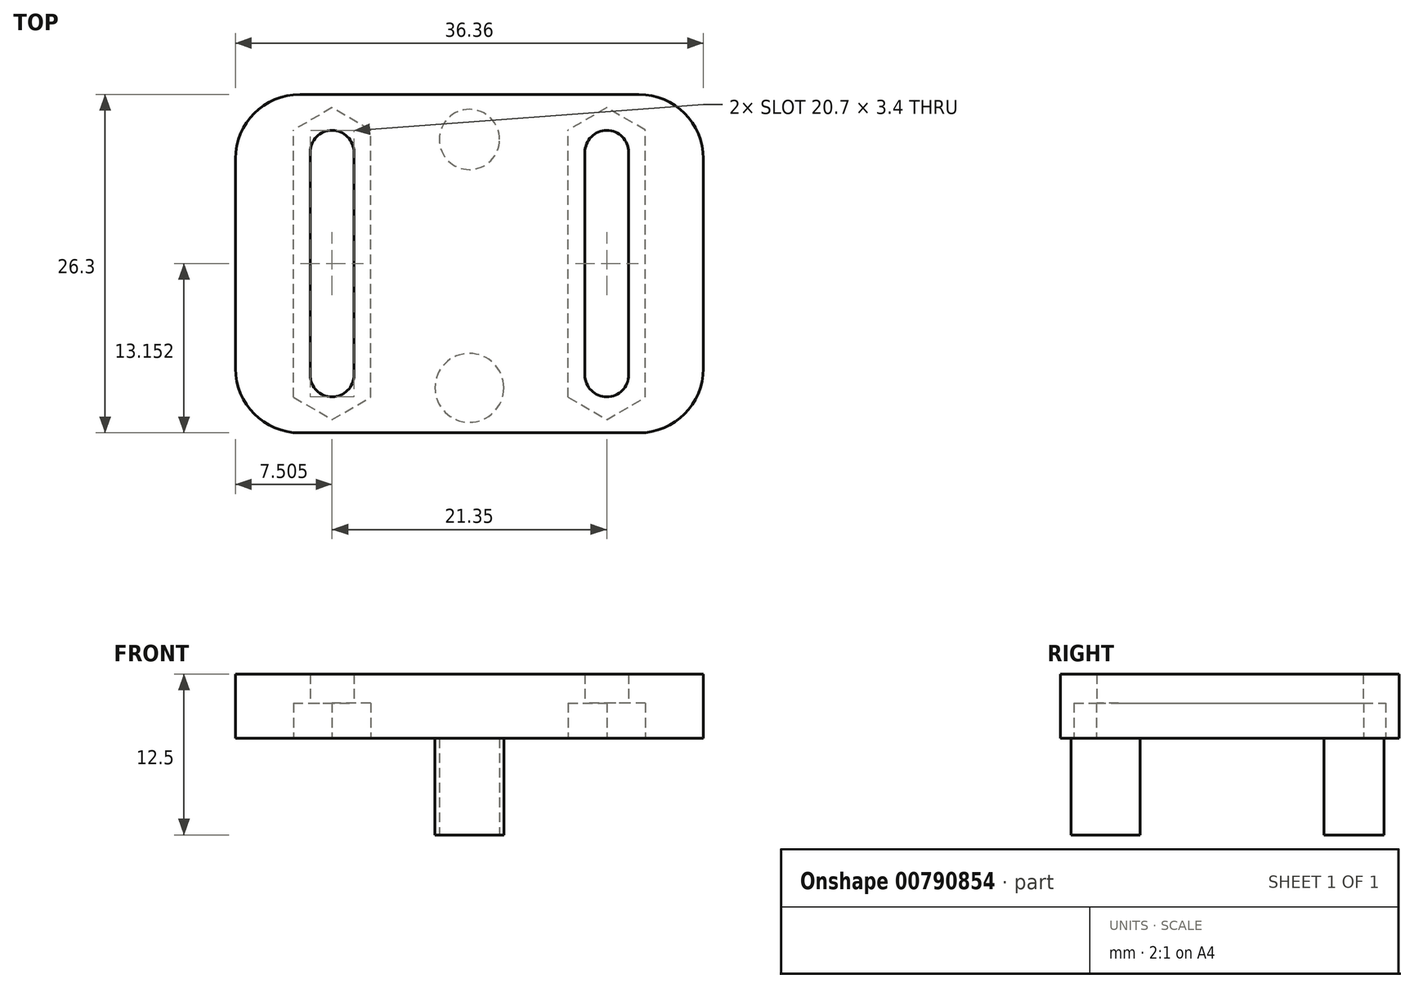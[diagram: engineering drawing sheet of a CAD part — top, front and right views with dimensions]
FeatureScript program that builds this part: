
annotation { "Feature Type Name" : "Feature", "Feature Type Description" : "" }
export const myFeature = defineFeature(function(context is Context, id is Id, definition is map)
    precondition{}
    {
        {
            var Q0;
            Q0=qCreatedBy(makeId("Top.planeOp"),FACE);
            var sketch = newSketch(context, id + "F0", { "sketchPlane" : qUnion([Q0])});
            skCircle(sketch, "E0", {"center": v(0, 0) * mm, "radius": 2.67 * mm});
            skCircle(sketch, "E1", {"center": v(0, 19.3) * mm, "radius": 2.34 * mm});
            skLineSegment(sketch, "E2.bottom", {"start": v(0, 9.65) * mm, "end": v(82.65, 9.65) * mm});
            skLineSegment(sketch, "E2.top", {"start": v(0, 230.05) * mm, "end": v(82.65, 230.05) * mm});
            skLineSegment(sketch, "E2.left", {"start": v(0, 9.65) * mm, "end": v(0, 230.05) * mm});
            skLineSegment(sketch, "E2.right", {"start": v(82.65, 9.65) * mm, "end": v(82.65, 230.05) * mm});
            skLineSegment(sketch, "E3", {"start": v(0, 19.3) * mm, "end": v(0, 0) * mm});
            skPoint(sketch, "E4", {"position": v(0, 9.65) * mm});
            skCircle(sketch, "E5.0.1.0", {"center": v(0, 239.7) * mm, "radius": 2.34 * mm});
            skCircle(sketch, "E5.0.1.1", {"center": v(0, 220.4) * mm, "radius": 2.67 * mm});
            skCircle(sketch, "E5.1.0.0", {"center": v(82.65, 19.3) * mm, "radius": 2.34 * mm});
            skCircle(sketch, "E5.1.0.1", {"center": v(82.65, 0) * mm, "radius": 2.67 * mm});
            skCircle(sketch, "E5.1.1.0", {"center": v(82.65, 239.7) * mm, "radius": 2.34 * mm});
            skCircle(sketch, "E5.1.1.1", {"center": v(82.65, 220.4) * mm, "radius": 2.67 * mm});
            skLineSegment(sketch, "E5.direction1", {"start": v(0, 19.3) * mm, "end": v(82.65, 19.3) * mm, "construction": true});
            skLineSegment(sketch, "E5.direction2", {"start": v(0, 19.3) * mm, "end": v(0, 239.7) * mm, "construction": true});
            skLineSegment(sketch, "E6.bottom", {"start": v(-10.68, 203.05) * mm, "end": v(93.32, 203.05) * mm});
            skLineSegment(sketch, "E6.top", {"start": v(-10.68, 35.05) * mm, "end": v(93.32, 35.05) * mm});
            skLineSegment(sketch, "E6.left", {"start": v(-10.68, 203.05) * mm, "end": v(-10.68, 35.05) * mm});
            skLineSegment(sketch, "E6.right", {"start": v(93.32, 203.05) * mm, "end": v(93.32, 35.05) * mm});
            skCircle(sketch, "E7.0.1.0", {"center": v(82.65, 27.55) * mm, "radius": 2.67 * mm});
            skCircle(sketch, "E7.0.1.1", {"center": v(82.65, 46.86) * mm, "radius": 2.34 * mm});
            skCircle(sketch, "E7.0.1.2", {"center": v(0, 46.85) * mm, "radius": 2.34 * mm});
            skCircle(sketch, "E7.0.1.3", {"center": v(0, 27.55) * mm, "radius": 2.67 * mm});
            skLineSegment(sketch, "E7.direction1", {"start": v(0, 0) * mm, "end": v(25, 0) * mm, "construction": true});
            skLineSegment(sketch, "E7.direction2", {"start": v(0, 0) * mm, "end": v(0, 27.55) * mm, "construction": true});
            skCircle(sketch, "E8.0.1.0", {"center": v(0, 192.85) * mm, "radius": 2.67 * mm});
            skCircle(sketch, "E8.0.1.1", {"center": v(82.65, 192.85) * mm, "radius": 2.67 * mm});
            skCircle(sketch, "E8.0.1.2", {"center": v(0, 212.16) * mm, "radius": 2.34 * mm});
            skCircle(sketch, "E8.0.1.3", {"center": v(82.65, 212.16) * mm, "radius": 2.34 * mm});
            skLineSegment(sketch, "E8.direction1", {"start": v(0, 220.4) * mm, "end": v(25, 220.4) * mm, "construction": true});
            skLineSegment(sketch, "E8.direction2", {"start": v(0, 220.4) * mm, "end": v(0, 192.85) * mm, "construction": true});
            skPoint(sketch, "E9", {"position": v(93.32, 37.75) * mm});
            skSolve(sketch);
        }
        {
            var Q0;
            Q0=qCreatedBy(makeId("Top.planeOp"),FACE);
            var sketch = newSketch(context, id + "F1", { "sketchPlane" : qUnion([Q0])});
            skCircle(sketch, "E10.0", {"center": v(0, 19.3) * mm, "radius": 2.34 * mm});
            skCircle(sketch, "E11.0", {"center": v(0, 0) * mm, "radius": 2.67 * mm});
            skSolve(sketch);
        }
        {
            var Q0;
            Q0=qSketchRegion(id+"F1",true);
            extrude(context, id + "F2", {"entities" : qUnion([Q0]), "depth" : 7.5 * mm, "offsetDistance" : 25 * mm});
        }
        {
            var Q0;
            Q0=makeQuery(id+"F2.opExtrude","CAP_FACE",FACE,{"disambiguationData":[OSD([sQuery(id+"F1.wireOp",EDGE,"E10.0")])],"isStart":false});
            var sketch = newSketch(context, id + "F3", { "sketchPlane" : qUnion([Q0])});
            skPoint(sketch, "E12.0", {"position": v(82.65, 27.55) * mm});
            skPoint(sketch, "E13.0", {"position": v(82.65, 46.86) * mm});
            skPoint(sketch, "E14.0", {"position": v(93.32, 37.75) * mm});
            skPoint(sketch, "E15.0", {"position": v(93.32, 35.05) * mm});
            skLineSegment(sketch, "E16.bottom", {"start": v(0, 22.8) * mm, "end": v(-10.68, 22.8) * mm});
            skLineSegment(sketch, "E16.top", {"start": v(0, -3.5) * mm, "end": v(-10.67, -3.5) * mm});
            skLineSegment(sketch, "E16.left", {"start": v(0, 22.8) * mm, "end": v(0, -3.5) * mm});
            skLineSegment(sketch, "E16.right", {"start": v(-10.68, 22.8) * mm, "end": v(-10.67, -3.5) * mm});
            skPoint(sketch, "E17", {"position": v(0, 19.3) * mm});
            skPoint(sketch, "E18", {"position": v(0, 0) * mm});
            skLineSegment(sketch, "E19.bottom", {"start": v(0, 22.8) * mm, "end": v(10.68, 22.8) * mm});
            skLineSegment(sketch, "E19.top", {"start": v(0, -3.5) * mm, "end": v(10.68, -3.5) * mm});
            skLineSegment(sketch, "E19.right", {"start": v(10.68, 22.8) * mm, "end": v(10.68, -3.5) * mm});
            skLineSegment(sketch, "E20.bottom", {"start": v(-10.68, 22.8) * mm, "end": v(-18.18, 22.8) * mm});
            skLineSegment(sketch, "E20.top", {"start": v(-10.67, -3.5) * mm, "end": v(-18.17, -3.5) * mm});
            skLineSegment(sketch, "E20.right", {"start": v(-18.18, 22.8) * mm, "end": v(-18.17, -3.5) * mm});
            skPoint(sketch, "E21", {"position": v(-10.67, 1) * mm});
            skPoint(sketch, "E22", {"position": v(-10.68, 18.3) * mm});
            skLineSegment(sketch, "E23.bottom", {"start": v(10.68, 22.8) * mm, "end": v(18.18, 22.8) * mm});
            skLineSegment(sketch, "E23.top", {"start": v(10.68, -3.5) * mm, "end": v(18.18, -3.5) * mm});
            skLineSegment(sketch, "E23.right", {"start": v(18.18, 22.8) * mm, "end": v(18.18, -3.5) * mm});
            skPoint(sketch, "E24", {"position": v(10.68, 1) * mm});
            skPoint(sketch, "E25", {"position": v(10.68, 18.3) * mm});
            skCircle(sketch, "E26", {"center": v(-10.68, 18.3) * mm, "radius": 1.7 * mm});
            skCircle(sketch, "E27", {"center": v(10.68, 18.3) * mm, "radius": 1.7 * mm});
            skCircle(sketch, "E28", {"center": v(10.68, 1) * mm, "radius": 1.7 * mm});
            skCircle(sketch, "E29", {"center": v(-10.67, 1) * mm, "radius": 1.7 * mm});
            skLineSegment(sketch, "E30", {"start": v(-8.97, 18.3) * mm, "end": v(-8.97, 1) * mm});
            skLineSegment(sketch, "E31", {"start": v(8.97, 18.3) * mm, "end": v(8.97, 1) * mm});
            skLineSegment(sketch, "E32", {"start": v(-12.37, 18.3) * mm, "end": v(-12.37, 1) * mm});
            skLineSegment(sketch, "E33", {"start": v(12.38, 1) * mm, "end": v(12.38, 18.3) * mm});
            skSolve(sketch);
        }
        {
            var Q0;
            Q0=makeQuery(id+"F3.imprint","IMPRINT",FACE,{"disambiguationData":[TD([[makeQuery(id+"F3.imprint","IMPRINT",EDGE,{"derivedFrom":makeQuery(id+"F2.opExtrude","CAP_EDGE",EDGE,{"disambiguationData":[OSD([sQuery(id+"F0.wireOp",EDGE,"E1")])],"isStart":false})}),-1.0]])]});
            var Q1;
            {var subQ0=sQuery(id+"F3.wireOp",EDGE,"TZnfkHZf-DKkp-xptn-AsGC-FlYiCB8cDqTM");Q1=makeQuery(id+"F3.imprint","IMPRINT",FACE,{"disambiguationData":[TD([[makeQuery(id+"F3.imprint","IMPRINT",EDGE,{"derivedFrom":subQ0}),-1.0]])]});}
            var Q2;
            {var subQ0=sQuery(id+"F3.wireOp",EDGE,"XSsqlgjZ-LNJ9-Avoh-l53S-mxeqoTWxBHOC");var subQ1=makeQuery(id+"F3.imprint","INTERSECT",VERTEX,{"derivedFrom":[subQ0,sQuery(id+"F3.wireOp",EDGE,"TZnfkHZf-DKkp-xptn-AsGC-FlYiCB8cDqTM")]});Q2=makeQuery(id+"F3.imprint","IMPRINT",FACE,{"disambiguationData":[TD([[makeQuery(id+"F3.imprint","IMPRINT",EDGE,{"disambiguationData":[TD([[subQ1,1.0]])],"derivedFrom":subQ0}),1.0]])]});}
            var Q3;
            Q3=makeQuery(id+"F3.imprint","IMPRINT",FACE,{"disambiguationData":[TD([[makeQuery(id+"F3.imprint","IMPRINT",EDGE,{"derivedFrom":makeQuery(id+"F2.opExtrude","CAP_EDGE",EDGE,{"disambiguationData":[OSD([sQuery(id+"F0.wireOp",EDGE,"E1")])],"isStart":false})}),1.0]])]});
            var Q4;
            Q4=makeQuery(id+"F3.imprint","IMPRINT",FACE,{"disambiguationData":[TD([[makeQuery(id+"F3.imprint","IMPRINT",EDGE,{"derivedFrom":sQuery(id+"F3.wireOp",EDGE,"hKwLHGTs-qPJH-S5hr-Gcpr-7g2Lq1g5tTZc.bottom")}),1.0]])]});
            var Q5;
            Q5=makeQuery(id+"F3.imprint","IMPRINT",FACE,{"disambiguationData":[TD([[makeQuery(id+"F3.imprint","IMPRINT",EDGE,{"derivedFrom":sQuery(id+"F3.wireOp",EDGE,"hKwLHGTs-qPJH-S5hr-Gcpr-7g2Lq1g5tTZc.bottom")}),-1.0]])]});
            var Q6;
            Q6=makeQuery(id+"F3.imprint","IMPRINT",FACE,{"disambiguationData":[TD([[makeQuery(id+"F3.imprint","IMPRINT",EDGE,{"derivedFrom":sQuery(id+"F3.wireOp",EDGE,"S0UTHaCf-9Zco-C6hI-kq23-d3yPxSgRmCOZ.bottom")}),1.0]])]});
            var Q7;
            Q7=makeQuery(id+"F3.imprint","IMPRINT",FACE,{"disambiguationData":[TD([[makeQuery(id+"F3.imprint","IMPRINT",EDGE,{"derivedFrom":makeQuery(id+"F2.opExtrude","CAP_EDGE",EDGE,{"disambiguationData":[OSD([sQuery(id+"F1.wireOp",EDGE,"E10.0")])],"isStart":false})}),1.0]])]});
            var Q8;
            {var subQ3=sQuery(id+"F3.wireOp",EDGE,"dA8Uuovx-4eO9-e5tU-pRAa-RQbBhlRNXynu.bottom");Q8=makeQuery(id+"F3.imprint","IMPRINT",FACE,{"disambiguationData":[TD([[makeQuery(id+"F3.imprint","IMPRINT",EDGE,{"derivedFrom":subQ3}),-1.0]])]});}
            var Q9;
            Q9=makeQuery(id+"F3.imprint","IMPRINT",FACE,{"disambiguationData":[TD([[makeQuery(id+"F3.imprint","IMPRINT",EDGE,{"derivedFrom":sQuery(id+"F3.wireOp",EDGE,"pLl2V4uJ-uvpy-u4wN-YW1n-wzNoaj7xdnqu.bottom")}),-1.0]])]});
            var Q10;
            Q10=makeQuery(id+"F3.imprint","IMPRINT",FACE,{"disambiguationData":[TD([[makeQuery(id+"F3.imprint","IMPRINT",EDGE,{"derivedFrom":sQuery(id+"F3.wireOp",EDGE,"rTHW2GkA-8Re8-zC11-azSP-cnDfZQFP3jBD.bottom")}),1.0]])]});
            var Q11;
            {var subQ3=sQuery(id+"F3.wireOp",EDGE,"04D0zXul-GAz9-AviL-uxYt-cow7iv5wdFvi.bottom");Q11=makeQuery(id+"F3.imprint","IMPRINT",FACE,{"disambiguationData":[TD([[makeQuery(id+"F3.imprint","IMPRINT",EDGE,{"derivedFrom":subQ3}),1.0]])]});}
            var Q12;
            {var subQ4=sQuery(id+"F3.wireOp",EDGE,"E19.bottom");Q12=makeQuery(id+"F3.imprint","IMPRINT",FACE,{"disambiguationData":[TD([[makeQuery(id+"F3.imprint","IMPRINT",EDGE,{"derivedFrom":subQ4}),-1.0]])]});}
            var Q13;
            {var subQ1=sQuery(id+"F3.wireOp",EDGE,"E16.bottom");Q13=makeQuery(id+"F3.imprint","IMPRINT",FACE,{"disambiguationData":[TD([[makeQuery(id+"F3.imprint","IMPRINT",EDGE,{"derivedFrom":subQ1}),1.0]])]});}
            var Q14;
            Q14=makeQuery(id+"F3.imprint","IMPRINT",FACE,{"disambiguationData":[TD([[makeQuery(id+"F3.imprint","IMPRINT",EDGE,{"derivedFrom":sQuery(id+"F3.wireOp",EDGE,"E20.bottom")}),1.0]])]});
            var Q15;
            Q15=makeQuery(id+"F3.imprint","IMPRINT",FACE,{"disambiguationData":[TD([[makeQuery(id+"F3.imprint","IMPRINT",EDGE,{"derivedFrom":sQuery(id+"F3.wireOp",EDGE,"E23.bottom")}),-1.0]])]});
            extrude(context, id + "F4", {"entities" : qUnion([Q0, Q1, Q2, Q3, Q4, Q5, Q6, Q7, Q8, Q9, Q10, Q11, Q12, Q13, Q14, Q15]), "depth" : 5 * mm, "offsetDistance" : 25 * mm});
        }
        {
            var Q0;
            Q0=makeQuery(id+"F4.opExtrude","SWEPT_EDGE",EDGE,{"disambiguationData":[OSD([sQuery(id+"F3.wireOp",EDGE,"hKwLHGTs-qPJH-S5hr-Gcpr-7g2Lq1g5tTZc.top"),sQuery(id+"F3.wireOp",EDGE,"hKwLHGTs-qPJH-S5hr-Gcpr-7g2Lq1g5tTZc.left")])]});
            var Q1;
            Q1=makeQuery(id+"F4.opExtrude","SWEPT_EDGE",EDGE,{"disambiguationData":[OSD([sQuery(id+"F3.wireOp",EDGE,"hKwLHGTs-qPJH-S5hr-Gcpr-7g2Lq1g5tTZc.top"),sQuery(id+"F3.wireOp",EDGE,"hKwLHGTs-qPJH-S5hr-Gcpr-7g2Lq1g5tTZc.right")])]});
            var Q2;
            Q2=makeQuery(id+"F4.opExtrude","SWEPT_EDGE",EDGE,{"disambiguationData":[OSD([sQuery(id+"F3.wireOp",EDGE,"S0UTHaCf-9Zco-C6hI-kq23-d3yPxSgRmCOZ.top"),sQuery(id+"F3.wireOp",EDGE,"S0UTHaCf-9Zco-C6hI-kq23-d3yPxSgRmCOZ.right")])]});
            var Q3;
            Q3=makeQuery(id+"F4.opExtrude","SWEPT_EDGE",EDGE,{"disambiguationData":[OSD([sQuery(id+"F3.wireOp",EDGE,"S0UTHaCf-9Zco-C6hI-kq23-d3yPxSgRmCOZ.top"),sQuery(id+"F3.wireOp",EDGE,"S0UTHaCf-9Zco-C6hI-kq23-d3yPxSgRmCOZ.left")])]});
            var Q4;
            Q4=makeQuery(id+"F4.opExtrude","SWEPT_EDGE",EDGE,{"disambiguationData":[OSD([sQuery(id+"F3.wireOp",EDGE,"pLl2V4uJ-uvpy-u4wN-YW1n-wzNoaj7xdnqu.bottom"),sQuery(id+"F3.wireOp",EDGE,"pLl2V4uJ-uvpy-u4wN-YW1n-wzNoaj7xdnqu.right")])]});
            var Q5;
            Q5=makeQuery(id+"F4.opExtrude","SWEPT_EDGE",EDGE,{"disambiguationData":[OSD([sQuery(id+"F3.wireOp",EDGE,"pLl2V4uJ-uvpy-u4wN-YW1n-wzNoaj7xdnqu.top"),sQuery(id+"F3.wireOp",EDGE,"pLl2V4uJ-uvpy-u4wN-YW1n-wzNoaj7xdnqu.right")])]});
            var Q6;
            Q6=makeQuery(id+"F4.opExtrude","SWEPT_EDGE",EDGE,{"disambiguationData":[OSD([sQuery(id+"F3.wireOp",EDGE,"rTHW2GkA-8Re8-zC11-azSP-cnDfZQFP3jBD.bottom"),sQuery(id+"F3.wireOp",EDGE,"rTHW2GkA-8Re8-zC11-azSP-cnDfZQFP3jBD.right")])]});
            var Q7;
            Q7=makeQuery(id+"F4.opExtrude","SWEPT_EDGE",EDGE,{"disambiguationData":[OSD([sQuery(id+"F3.wireOp",EDGE,"rTHW2GkA-8Re8-zC11-azSP-cnDfZQFP3jBD.top"),sQuery(id+"F3.wireOp",EDGE,"rTHW2GkA-8Re8-zC11-azSP-cnDfZQFP3jBD.right")])]});
            var Q8;
            Q8=makeQuery(id+"F4.opExtrude","SWEPT_EDGE",EDGE,{"disambiguationData":[OSD([sQuery(id+"F3.wireOp",EDGE,"E20.bottom"),sQuery(id+"F3.wireOp",EDGE,"E20.right")])]});
            var Q9;
            Q9=makeQuery(id+"F4.opExtrude","SWEPT_EDGE",EDGE,{"disambiguationData":[OSD([sQuery(id+"F3.wireOp",EDGE,"E20.top"),sQuery(id+"F3.wireOp",EDGE,"E20.right")])]});
            var Q10;
            Q10=makeQuery(id+"F4.opExtrude","SWEPT_EDGE",EDGE,{"disambiguationData":[OSD([sQuery(id+"F3.wireOp",EDGE,"E19.top"),sQuery(id+"F3.wireOp",EDGE,"E19.right")])]});
            var Q11;
            Q11=makeQuery(id+"F4.opExtrude","SWEPT_EDGE",EDGE,{"disambiguationData":[OSD([sQuery(id+"F3.wireOp",EDGE,"E19.bottom"),sQuery(id+"F3.wireOp",EDGE,"E19.right")])]});
            var Q12;
            Q12=makeQuery(id+"F4.opExtrude","SWEPT_EDGE",EDGE,{"disambiguationData":[OSD([sQuery(id+"F3.wireOp",EDGE,"E23.top"),sQuery(id+"F3.wireOp",EDGE,"E23.right")])]});
            var Q13;
            Q13=makeQuery(id+"F4.opExtrude","SWEPT_EDGE",EDGE,{"disambiguationData":[OSD([sQuery(id+"F3.wireOp",EDGE,"E23.bottom"),sQuery(id+"F3.wireOp",EDGE,"E23.right")])]});
            fillet(context, id + "F5", {"entities" : qUnion([Q0, Q1, Q2, Q3, Q4, Q5, Q6, Q7, Q8, Q9, Q10, Q11, Q12, Q13]), "tangentPropagation" : true, "radius" : 5 * mm, "defaultsChanged" : false, "vertexSettings" : [], "allowEdgeOverflow" : false});
        }
        {
            var Q0;
            Q0=makeQuery(id+"F4.opExtrude","CAP_FACE",FACE,{"disambiguationData":[OSD([sQuery(id+"F3.wireOp",EDGE,"E16.bottom"),sQuery(id+"F3.wireOp",EDGE,"E16.top"),sQuery(id+"F3.wireOp",EDGE,"E19.bottom"),sQuery(id+"F3.wireOp",EDGE,"E19.top"),sQuery(id+"F3.wireOp",EDGE,"E19.right"),sQuery(id+"F3.wireOp",EDGE,"E20.bottom"),sQuery(id+"F3.wireOp",EDGE,"E20.top"),sQuery(id+"F3.wireOp",EDGE,"E20.right")])],"isStart":true});
            var sketch = newSketch(context, id + "F6", { "sketchPlane" : qUnion([Q0])});
            skCircle(sketch, "E34.cCircle", {"center": v(-10.67, -1) * mm, "radius": 3 * mm, "construction": true});
            skLineSegment(sketch, "E34.0", {"start": v(-10.67, 2.46) * mm, "end": v(-7.68, 0.73) * mm});
            skLineSegment(sketch, "E34.1", {"start": v(-7.68, 0.73) * mm, "end": v(-7.68, -2.73) * mm});
            skLineSegment(sketch, "E34.2", {"start": v(-7.67, -2.73) * mm, "end": v(-10.67, -4.46) * mm});
            skLineSegment(sketch, "E34.3", {"start": v(-10.67, -4.46) * mm, "end": v(-13.67, -2.73) * mm});
            skLineSegment(sketch, "E34.4", {"start": v(-13.67, -2.73) * mm, "end": v(-13.67, 0.73) * mm});
            skLineSegment(sketch, "E34.5", {"start": v(-13.67, 0.73) * mm, "end": v(-10.67, 2.46) * mm});
            skCircle(sketch, "E35.cCircle", {"center": v(-10.68, -18.3) * mm, "radius": 3 * mm, "construction": true});
            skLineSegment(sketch, "E35.0", {"start": v(-10.68, -14.84) * mm, "end": v(-7.68, -16.57) * mm});
            skLineSegment(sketch, "E35.1", {"start": v(-7.68, -16.57) * mm, "end": v(-7.68, -20.04) * mm});
            skLineSegment(sketch, "E35.2", {"start": v(-7.68, -20.04) * mm, "end": v(-10.68, -21.77) * mm});
            skLineSegment(sketch, "E35.3", {"start": v(-10.68, -21.77) * mm, "end": v(-13.68, -20.04) * mm});
            skLineSegment(sketch, "E35.4", {"start": v(-13.67, -20.04) * mm, "end": v(-13.67, -16.57) * mm});
            skLineSegment(sketch, "E35.5", {"start": v(-13.67, -16.57) * mm, "end": v(-10.68, -14.84) * mm});
            skCircle(sketch, "E36.cCircle", {"center": v(10.68, -1) * mm, "radius": 3 * mm, "construction": true});
            skPoint(sketch, "E36.cCircle.perimeterSnap0", {"position": v(10.67, -5.8) * mm});
            skLineSegment(sketch, "E36.0", {"start": v(7.68, 0.73) * mm, "end": v(10.68, 2.46) * mm});
            skLineSegment(sketch, "E36.1", {"start": v(10.68, 2.46) * mm, "end": v(13.68, 0.73) * mm});
            skLineSegment(sketch, "E36.2", {"start": v(13.68, 0.73) * mm, "end": v(13.67, -2.73) * mm});
            skLineSegment(sketch, "E36.3", {"start": v(13.67, -2.73) * mm, "end": v(10.67, -4.46) * mm});
            skLineSegment(sketch, "E36.4", {"start": v(10.67, -4.46) * mm, "end": v(7.67, -2.73) * mm});
            skLineSegment(sketch, "E36.5", {"start": v(7.67, -2.73) * mm, "end": v(7.68, 0.73) * mm});
            skPoint(sketch, "E36.0.midPoint", {"position": v(9.18, 1.6) * mm});
            skPoint(sketch, "E36.0.midPoint.positionSnap0", {"position": v(9.18, 0.47) * mm});
            skCircle(sketch, "E37.cCircle", {"center": v(10.68, -18.3) * mm, "radius": 3 * mm, "construction": true});
            skPoint(sketch, "E37.cCircle.perimeterSnap0", {"position": v(12.17, -3.6) * mm});
            skLineSegment(sketch, "E37.0", {"start": v(10.68, -14.84) * mm, "end": v(13.68, -16.57) * mm});
            skLineSegment(sketch, "E37.1", {"start": v(13.68, -16.57) * mm, "end": v(13.68, -20.04) * mm});
            skLineSegment(sketch, "E37.2", {"start": v(13.68, -20.04) * mm, "end": v(10.68, -21.77) * mm});
            skLineSegment(sketch, "E37.3", {"start": v(10.68, -21.77) * mm, "end": v(7.68, -20.04) * mm});
            skLineSegment(sketch, "E37.4", {"start": v(7.68, -20.04) * mm, "end": v(7.68, -16.57) * mm});
            skLineSegment(sketch, "E37.5", {"start": v(7.68, -16.57) * mm, "end": v(10.68, -14.84) * mm});
            skPoint(sketch, "E37.0.midPoint", {"position": v(12.18, -15.7) * mm});
            skPoint(sketch, "E37.0.midPoint.positionSnap0", {"position": v(12.17, -3.6) * mm});
            skLineSegment(sketch, "E38", {"start": v(-13.67, -2.73) * mm, "end": v(-13.67, -16.57) * mm});
            skLineSegment(sketch, "E39", {"start": v(-7.67, -2.73) * mm, "end": v(-7.68, -16.57) * mm});
            skLineSegment(sketch, "E40", {"start": v(7.67, -2.73) * mm, "end": v(7.68, -16.57) * mm});
            skLineSegment(sketch, "E41", {"start": v(13.67, -2.73) * mm, "end": v(13.68, -16.57) * mm});
            skSolve(sketch);
        }
        {
            var Q0;
            Q0=qSketchRegion(id+"F6",true);
            extrude(context, id + "F7", {"entities" : qUnion([Q0]), "operationType" : NewBodyOperationType.REMOVE, "oppositeDirection" : true, "depth" : 2.75 * mm, "offsetDistance" : 25 * mm});
        }
    });
